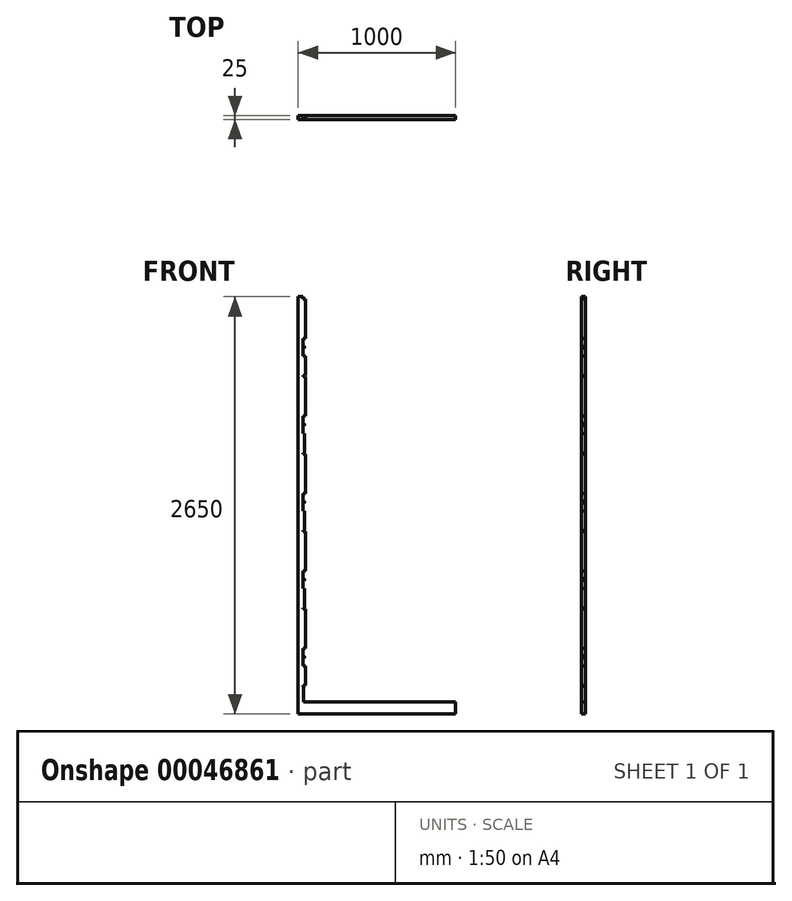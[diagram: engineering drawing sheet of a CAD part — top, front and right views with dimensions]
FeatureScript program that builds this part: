
annotation { "Feature Type Name" : "Feature", "Feature Type Description" : "" }
export const myFeature = defineFeature(function(context is Context, id is Id, definition is map)
    precondition{}
    {
        {
            var Q0;
            Q0=qCreatedBy(makeId("Front.planeOp"),FACE);
            var sketch = newSketch(context, id + "F0", { "sketchPlane" : qUnion([Q0])});
            skLineSegment(sketch, "E0.bottom", {"start": v(0, 0) * mm, "end": v(30, 0) * mm});
            skLineSegment(sketch, "E0.top", {"start": v(0, 2575) * mm, "end": v(30, 2575) * mm});
            skLineSegment(sketch, "E0.left", {"start": v(0, 0) * mm, "end": v(0, 2575) * mm});
            skLineSegment(sketch, "E0.right", {"start": v(30, 0) * mm, "end": v(30, 2575) * mm});
            skLineSegment(sketch, "E1.bottom", {"start": v(0, 0) * mm, "end": v(1000, 0) * mm});
            skLineSegment(sketch, "E1.top", {"start": v(0, -75) * mm, "end": v(1000, -75) * mm});
            skLineSegment(sketch, "E1.left", {"start": v(0, 0) * mm, "end": v(0, -75) * mm});
            skLineSegment(sketch, "E1.right", {"start": v(1000, 0) * mm, "end": v(1000, -75) * mm});
            skLineSegment(sketch, "E2.bottom", {"start": v(30, 0) * mm, "end": v(33, 0) * mm});
            skLineSegment(sketch, "E2.top", {"start": v(30, 100) * mm, "end": v(33, 100) * mm});
            skLineSegment(sketch, "E2.left", {"start": v(30, 0) * mm, "end": v(30, 100) * mm});
            skLineSegment(sketch, "E2.right", {"start": v(33, 0) * mm, "end": v(33, 100) * mm});
            skLineSegment(sketch, "E3.bottom", {"start": v(30, 105) * mm, "end": v(46, 105) * mm});
            skLineSegment(sketch, "E3.top", {"start": v(30, 230) * mm, "end": v(46, 230) * mm});
            skLineSegment(sketch, "E3.left", {"start": v(30, 105) * mm, "end": v(30, 230) * mm});
            skLineSegment(sketch, "E3.right", {"start": v(46, 105) * mm, "end": v(46, 230) * mm});
            skLineSegment(sketch, "E4.bottom", {"start": v(30, 342) * mm, "end": v(46, 342) * mm});
            skLineSegment(sketch, "E4.top", {"start": v(30, 592) * mm, "end": v(46, 592) * mm});
            skLineSegment(sketch, "E4.left", {"start": v(30, 342) * mm, "end": v(30, 592) * mm});
            skLineSegment(sketch, "E4.right", {"start": v(46, 342) * mm, "end": v(46, 592) * mm});
            skLineSegment(sketch, "E5.bottom", {"start": v(30, 597) * mm, "end": v(42, 597) * mm});
            skLineSegment(sketch, "E5.top", {"start": v(30, 722) * mm, "end": v(42, 722) * mm});
            skLineSegment(sketch, "E5.left", {"start": v(30, 597) * mm, "end": v(30, 722) * mm});
            skLineSegment(sketch, "E5.right", {"start": v(42, 597) * mm, "end": v(42, 722) * mm});
            skCircle(sketch, "E6", {"center": v(36, 778) * mm, "radius": 6 * mm});
            skLineSegment(sketch, "E7.bottom", {"start": v(30, 834) * mm, "end": v(46, 834) * mm});
            skLineSegment(sketch, "E7.top", {"start": v(30, 1084) * mm, "end": v(46, 1084) * mm});
            skLineSegment(sketch, "E7.left", {"start": v(30, 834) * mm, "end": v(30, 1084) * mm});
            skLineSegment(sketch, "E7.right", {"start": v(46, 834) * mm, "end": v(46, 1084) * mm});
            skCircle(sketch, "E8", {"center": v(36, 286) * mm, "radius": 6 * mm});
            skLineSegment(sketch, "E9.bottom", {"start": v(30, 1089) * mm, "end": v(42, 1089) * mm});
            skLineSegment(sketch, "E9.top", {"start": v(30, 1214) * mm, "end": v(42, 1214) * mm});
            skLineSegment(sketch, "E9.left", {"start": v(30, 1089) * mm, "end": v(30, 1214) * mm});
            skLineSegment(sketch, "E9.right", {"start": v(42, 1089) * mm, "end": v(42, 1214) * mm});
            skCircle(sketch, "E10", {"center": v(36, 1270) * mm, "radius": 6 * mm});
            skLineSegment(sketch, "E11.bottom", {"start": v(30, 1326) * mm, "end": v(46, 1326) * mm});
            skLineSegment(sketch, "E11.top", {"start": v(30, 1576) * mm, "end": v(46, 1576) * mm});
            skLineSegment(sketch, "E11.left", {"start": v(30, 1326) * mm, "end": v(30, 1576) * mm});
            skLineSegment(sketch, "E11.right", {"start": v(46, 1326) * mm, "end": v(46, 1576) * mm});
            skLineSegment(sketch, "E12.bottom", {"start": v(30, 1581) * mm, "end": v(42, 1581) * mm});
            skLineSegment(sketch, "E12.top", {"start": v(30, 1706) * mm, "end": v(42, 1706) * mm});
            skLineSegment(sketch, "E12.left", {"start": v(30, 1581) * mm, "end": v(30, 1706) * mm});
            skLineSegment(sketch, "E12.right", {"start": v(42, 1581) * mm, "end": v(42, 1706) * mm});
            skCircle(sketch, "E13", {"center": v(36, 1762) * mm, "radius": 6 * mm});
            skLineSegment(sketch, "E14.bottom", {"start": v(30, 1818) * mm, "end": v(46, 1818) * mm});
            skLineSegment(sketch, "E14.top", {"start": v(30, 2068) * mm, "end": v(46, 2068) * mm});
            skLineSegment(sketch, "E14.left", {"start": v(30, 1818) * mm, "end": v(30, 2068) * mm});
            skLineSegment(sketch, "E14.right", {"start": v(46, 1818) * mm, "end": v(46, 2068) * mm});
            skLineSegment(sketch, "E15.bottom", {"start": v(30, 2073) * mm, "end": v(46, 2073) * mm});
            skLineSegment(sketch, "E15.top", {"start": v(30, 2198) * mm, "end": v(46, 2198) * mm});
            skLineSegment(sketch, "E15.left", {"start": v(30, 2073) * mm, "end": v(30, 2198) * mm});
            skLineSegment(sketch, "E15.right", {"start": v(46, 2073) * mm, "end": v(46, 2198) * mm});
            skCircle(sketch, "E16", {"center": v(36, 2254) * mm, "radius": 6 * mm});
            skLineSegment(sketch, "E17.bottom", {"start": v(30, 2310) * mm, "end": v(46, 2310) * mm});
            skLineSegment(sketch, "E17.top", {"start": v(30, 2560) * mm, "end": v(46, 2560) * mm});
            skLineSegment(sketch, "E17.left", {"start": v(30, 2310) * mm, "end": v(30, 2560) * mm});
            skLineSegment(sketch, "E17.right", {"start": v(46, 2310) * mm, "end": v(46, 2560) * mm});
            skSolve(sketch);
        }
        {
            var Q0;
            Q0 = qSketchRegion(id + "F0", true);
            extrude(context, id + "F1", {"entities" : qUnion([Q0]), "depth" : 25 * mm});
        }
    });
